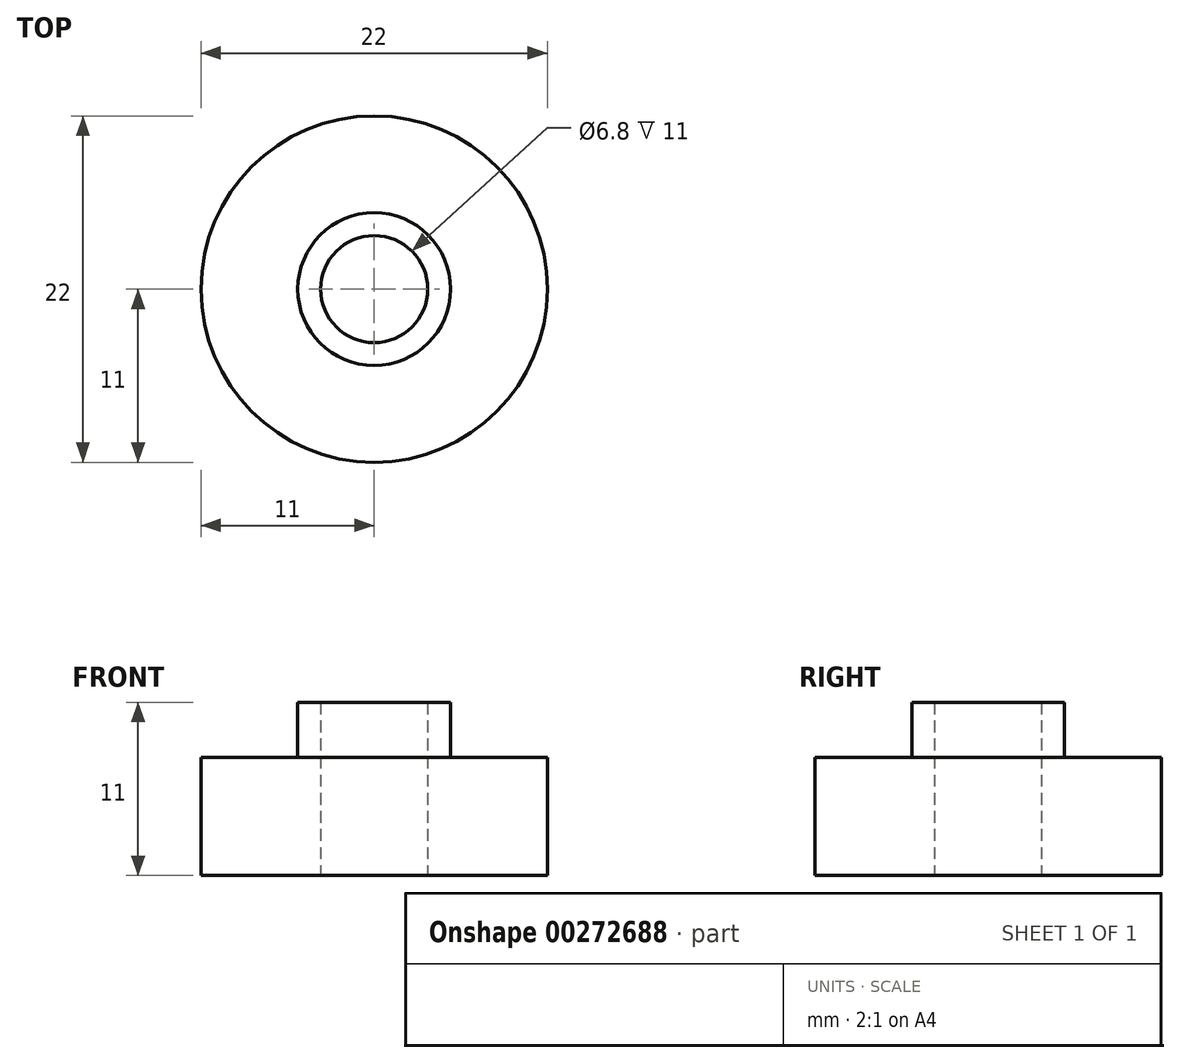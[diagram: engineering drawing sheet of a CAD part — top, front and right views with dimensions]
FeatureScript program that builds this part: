
annotation { "Feature Type Name" : "Feature", "Feature Type Description" : "" }
export const myFeature = defineFeature(function(context is Context, id is Id, definition is map)
    precondition{}
    {
        {
            var Q0;
            Q0=qCreatedBy(makeId("Top.planeOp"),FACE);
            var sketch = newSketch(context, id + "F0", { "sketchPlane" : qUnion([Q0])});
            skCircle(sketch, "E0", {"center": v(0, 0) * mm, "radius": 11 * mm});
            skCircle(sketch, "E1", {"center": v(0, 0) * mm, "radius": 4.85 * mm});
            skSolve(sketch);
        }
        {
            var Q0;
            Q0 = qSketchRegion(id + "F0", true);
            var Q1;
            Q1=makeQuery(id+"F0.imprint","IMPRINT",FACE,{"disambiguationData":[TD([[makeQuery(id+"F0.imprint","IMPRINT",EDGE,{"derivedFrom":sQuery(id+"F0.wireOp",EDGE,"E1")}),1.0]])]});
            extrude(context, id + "F1", {"entities" : qUnion([Q0, Q1]), "depth" : 7.5 * mm, "offsetDistance" : 25 * mm});
        }
        {
            var Q0;
            Q0=makeQuery(id+"F0.imprint","IMPRINT",FACE,{"disambiguationData":[TD([[makeQuery(id+"F0.imprint","IMPRINT",EDGE,{"derivedFrom":sQuery(id+"F0.wireOp",EDGE,"E1")}),1.0]])]});
            extrude(context, id + "F2", {"entities" : qUnion([Q0]), "operationType" : NewBodyOperationType.ADD, "depth" : 11 * mm, "offsetDistance" : 25 * mm});
        }
        {
            var Q0;
            Q0=sQuery(id+"F0.wireOp",VERTEX,"E0.center");
            var Q1;
            Q1=makeQuery(id+"F1.opExtrude","SWEPT_BODY",BODY,{"disambiguationData":[OSD([sQuery(id+"F0.wireOp",EDGE,"E0")])]});
            hole(context, id + "F3", {"style" : HoleStyle.SIMPLE, "endStyle" : HoleEndStyle.THROUGH, "oppositeDirection" : true, "standardTappedOrClearance" : lookupTablePath({ "standard" : "ISO", "engagement" : "75%", "pitch" : "1.25 mm", "size" : "M8", "type" : "Tapped" }), "standardBlindInLast" : lookupTablePath({ "standard" : "ISO", "engagement" : "75%", "pitch" : "1.25 mm", "size" : "M8", "type" : "Tapped" }), "holeDiameter" : 6.8 * mm, "majorDiameter" : 8 * mm, "showTappedDepth" : true, "isTappedThrough" : true, "tappedDepth" : 12 * mm, "tapClearance" : 3, "locations" : qUnion([Q0]), "scope" : qUnion([Q1])});
        }
    });
